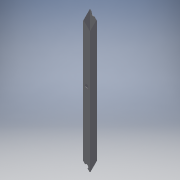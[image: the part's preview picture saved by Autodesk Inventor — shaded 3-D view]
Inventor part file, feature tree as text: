
AUTODESK INVENTOR PART (.ipt)
format: ipt  version: 2016 (Build 200138000, 138)  size: 136,704 bytes
history: native  units: in
note: dims shown in document units (in); Inventor stores cm internally (conversion verified against a paired STEP export)
features: extrude x5, sketch x5
ambient origin geometry x8: Origin, YZ Plane, XZ Plane, XY Plane, X Axis, Y Axis, Z Axis, Center Point
bodies: Solid1 (feature_tree)
feature tree (10):
  extrude  "Extrusion1"  Depth=1.0in
  extrude  "Extrusion4"  Depth=0.0625in TaperAngle=0.0deg
  extrude  "Extrusion5"  Depth=0.5in
  extrude  "Extrusion6"  Depth=1.0in TaperAngle=0.0deg
  extrude  "Extrusion7"  Depth=1.0in
  sketch  "Sketch1"  dims[d0=1.0in d1=1.0in]
  sketch  "Sketch4"  dims[d2=0.0625in d3=15.982in d4=0.0in]
  sketch  "Sketch5"  dims[d13=0.5in d14=0.5in]
  sketch  "Sketch6"  dims[d15=7.0in d16=1.0in d17=0.0in]
  sketch  "Sketch7"  dims[d19=1.5in d20=0.0in d21=0.5in d22=0.5in d23=0.5in d24=1.5in d25=0.0in d26=0.5in d29=1.0in d30=0.0in d31=0.5in d32=0.5in]
